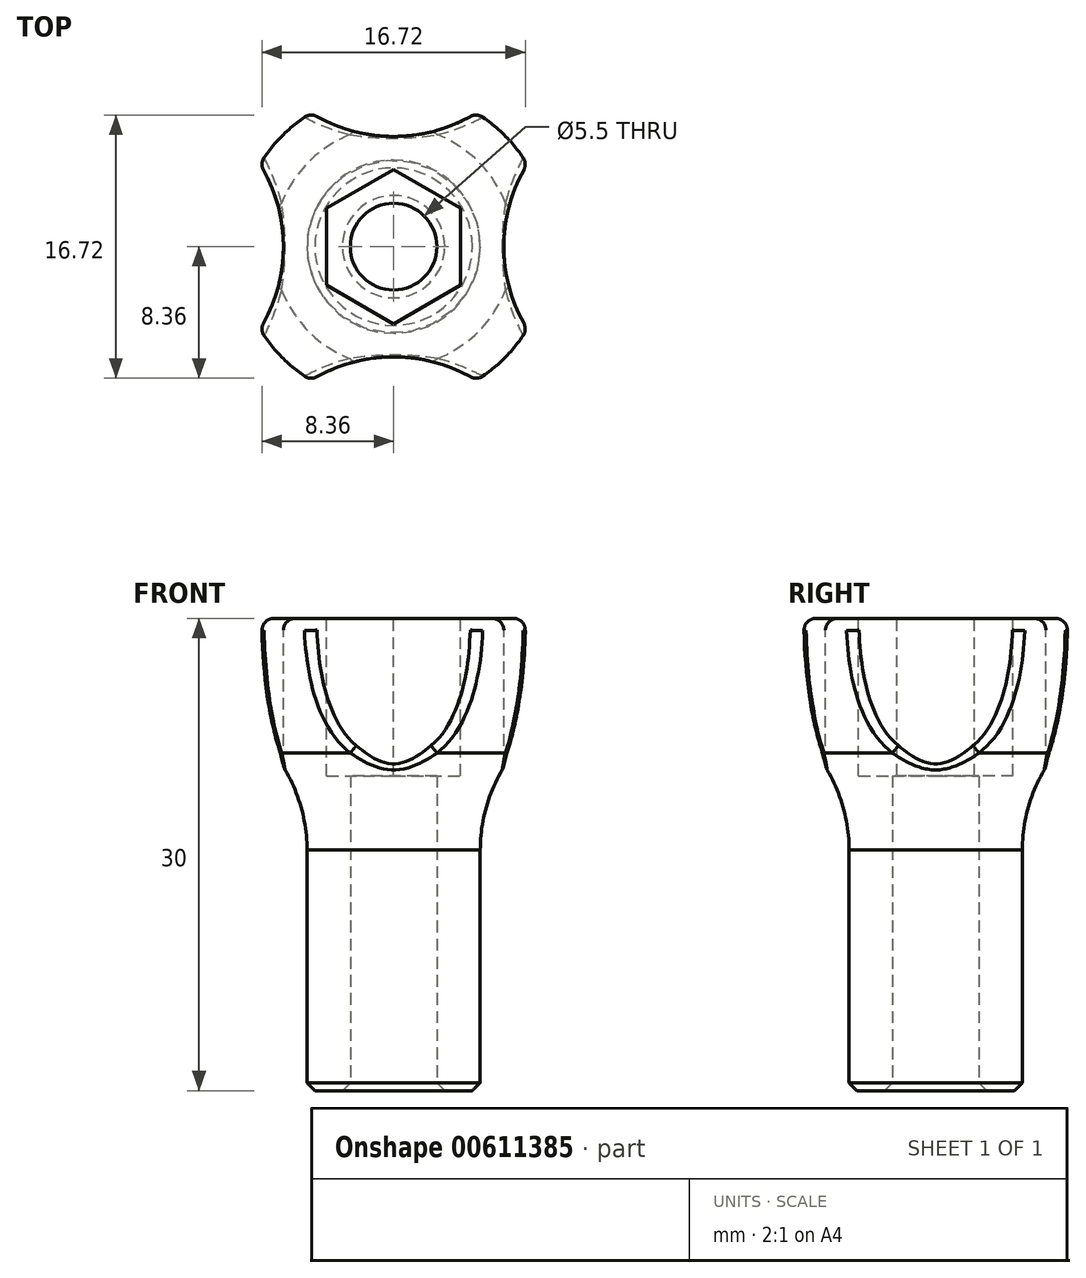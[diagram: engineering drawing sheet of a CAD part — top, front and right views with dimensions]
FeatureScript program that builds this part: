
annotation { "Feature Type Name" : "Feature", "Feature Type Description" : "" }
export const myFeature = defineFeature(function(context is Context, id is Id, definition is map)
    precondition{}
    {
        {
            var Q0;
            Q0=qCreatedBy(makeId("Top.planeOp"),FACE);
            cPlane(context, id + "F0", {"entities" : qUnion([Q0]), "cplaneType" : CPlaneType.OFFSET, "offset" : 30 * mm, "width" : 150 * mm, "height" : 150 * mm});
        }
        {
            var Q0;
            Q0=qCreatedBy(makeId("Top.planeOp"),FACE);
            var sketch = newSketch(context, id + "F1", { "sketchPlane" : qUnion([Q0])});
            skCircle(sketch, "E0", {"center": v(0, 0) * mm, "radius": 2.75 * mm});
            skCircle(sketch, "E1", {"center": v(0, 0) * mm, "radius": 5.5 * mm});
            skSolve(sketch);
        }
        {
            var Q0;
            Q0=makeQuery(id+"F1.imprint","IMPRINT",FACE,{"disambiguationData":[TD([[makeQuery(id+"F1.imprint","IMPRINT",EDGE,{"derivedFrom":sQuery(id+"F1.wireOp",EDGE,"E0")}),-1.0]])]});
            extrude(context, id + "F2", {"entities" : qUnion([Q0]), "depth" : 20 * mm, "offsetDistance" : 25 * mm});
        }
        {
            var Q0;
            Q0=makeQuery(id+"F2.opExtrude","CAP_FACE",FACE,{"disambiguationData":[OSD([sQuery(id+"F1.wireOp",EDGE,"E0"),sQuery(id+"F1.wireOp",EDGE,"E1")])],"isStart":false});
            var sketch = newSketch(context, id + "F3", { "sketchPlane" : qUnion([Q0])});
            skCircle(sketch, "E2", {"center": v(0, 0) * mm, "radius": 5.5 * mm});
            skSolve(sketch);
        }
        {
            var Q0;
            Q0=qCreatedBy(id+"F0.planeOp",FACE);
            var sketch = newSketch(context, id + "F4", { "sketchPlane" : qUnion([Q0])});
            skCircle(sketch, "E3", {"center": v(0, 0) * mm, "radius": 10 * mm});
            skSolve(sketch);
        }
        {
            var Q1;
            Q1 = qSketchRegion(id + "F4", true);
            var Q2;
            Q2 = qSketchRegion(id + "F3", true);
            loft(context, id + "F5", {"operationType" : NewBodyOperationType.ADD, "startCondition" : LoftEndDerivativeType.NORMAL_TO_PROFILE, "startMagnitude" : 2, "endCondition" : LoftEndDerivativeType.TANGENT_TO_PROFILE, "endMagnitude" : 1, "sheetProfilesArray" : [{ "sheetProfileEntities" : qUnion([Q1]) }, { "sheetProfileEntities" : qUnion([Q2]) }]});
        }
        {
            var Q0;
            Q0=makeQuery(id+"F5.boolean.opBoolean","MERGE",EDGE,{"derivedFrom":[makeQuery(id+"F2.opExtrude","CAP_EDGE",EDGE,{"disambiguationData":[OSD([sQuery(id+"F1.wireOp",EDGE,"E1")])],"isStart":false}),makeQuery(id+"F5.opLoft","MID_CAP_EDGE",EDGE,{"disambiguationData":[OSD([sQuery(id+"F3.wireOp",EDGE,"E2")])],"capPos":1.0})]});
            fillet(context, id + "F6", {"entities" : qUnion([Q0]), "radius" : 10 * mm, "tangentPropagation" : true, "allowEdgeOverflow" : false});
        }
        {
            var Q0;
            Q0=qCreatedBy(id+"F0.planeOp",FACE);
            var sketch = newSketch(context, id + "F7", { "sketchPlane" : qUnion([Q0])});
            skCircle(sketch, "E4", {"center": v(0, 17) * mm, "radius": 10 * mm});
            skCircle(sketch, "E5.1.0", {"center": v(-17, 0) * mm, "radius": 10 * mm});
            skCircle(sketch, "E5.2.0", {"center": v(0, -17) * mm, "radius": 10 * mm});
            skCircle(sketch, "E5.3.0", {"center": v(17, 0) * mm, "radius": 10 * mm});
            skPoint(sketch, "E5.center", {"position": v(0, 0) * mm});
            skCircle(sketch, "E6.cCircle", {"center": v(0, 0) * mm, "radius": 4.25 * mm, "construction": true});
            skLineSegment(sketch, "E6.0", {"start": v(4.25, 2.45) * mm, "end": v(4.25, -2.45) * mm});
            skLineSegment(sketch, "E6.1", {"start": v(4.25, -2.45) * mm, "end": v(0, -4.9) * mm});
            skLineSegment(sketch, "E6.2", {"start": v(0, -4.9) * mm, "end": v(-4.25, -2.45) * mm});
            skLineSegment(sketch, "E6.3", {"start": v(-4.25, -2.45) * mm, "end": v(-4.25, 2.45) * mm});
            skLineSegment(sketch, "E6.4", {"start": v(-4.25, 2.45) * mm, "end": v(0, 4.9) * mm});
            skLineSegment(sketch, "E6.5", {"start": v(0, 4.9) * mm, "end": v(4.25, 2.45) * mm});
            skPoint(sketch, "E6.0.midPoint", {"position": v(4.25, 0) * mm});
            skSolve(sketch);
        }
        {
            var Q0;
            Q0=makeQuery(id+"F7.imprint","IMPRINT",FACE,{"disambiguationData":[TD([[makeQuery(id+"F7.imprint","IMPRINT",EDGE,{"derivedFrom":sQuery(id+"F7.wireOp",EDGE,"E5.1.0")}),1.0]])]});
            var Q1;
            Q1=makeQuery(id+"F7.imprint","IMPRINT",FACE,{"disambiguationData":[TD([[makeQuery(id+"F7.imprint","IMPRINT",EDGE,{"derivedFrom":sQuery(id+"F7.wireOp",EDGE,"E4")}),1.0]])]});
            var Q2;
            Q2=makeQuery(id+"F7.imprint","IMPRINT",FACE,{"disambiguationData":[TD([[makeQuery(id+"F7.imprint","IMPRINT",EDGE,{"derivedFrom":sQuery(id+"F7.wireOp",EDGE,"E5.3.0")}),1.0]])]});
            var Q3;
            Q3=makeQuery(id+"F7.imprint","IMPRINT",FACE,{"disambiguationData":[TD([[makeQuery(id+"F7.imprint","IMPRINT",EDGE,{"derivedFrom":sQuery(id+"F7.wireOp",EDGE,"E5.2.0")}),1.0]])]});
            extrude(context, id + "F8", {"entities" : qUnion([Q0, Q1, Q2, Q3]), "operationType" : NewBodyOperationType.REMOVE, "oppositeDirection" : true, "depth" : 25 * mm, "offsetDistance" : 25 * mm});
        }
        {
            var Q0;
            Q0=makeQuery(id+"F7.imprint","IMPRINT",FACE,{"disambiguationData":[TD([[makeQuery(id+"F7.imprint","IMPRINT",EDGE,{"derivedFrom":sQuery(id+"F7.wireOp",EDGE,"E6.0")}),-1.0]])]});
            extrude(context, id + "F9", {"entities" : qUnion([Q0]), "operationType" : NewBodyOperationType.REMOVE, "oppositeDirection" : true, "depth" : 10 * mm, "offsetDistance" : 25 * mm});
        }
        {
            var Q0;
            Q0=makeQuery(id+"F2.opExtrude","CAP_FACE",FACE,{"disambiguationData":[OSD([sQuery(id+"F1.wireOp",EDGE,"E0"),sQuery(id+"F1.wireOp",EDGE,"E1")])],"isStart":true});
            chamfer(context, id + "F10", {"entities" : qUnion([Q0]), "width" : .5 * mm, "tangentPropagation" : true});
        }
        {
            var Q0;
            Q0=makeQuery(id+"F8.boolean.opBoolean","COPY",FACE,{"derivedFrom":makeQuery(id+"F8.opExtrude","SWEPT_FACE",FACE,{"disambiguationData":[OSD([sQuery(id+"F7.wireOp",EDGE,"E5.2.0")])]})});
            var Q1;
            Q1=makeQuery(id+"F8.boolean.opBoolean","COPY",FACE,{"derivedFrom":makeQuery(id+"F8.opExtrude","SWEPT_FACE",FACE,{"disambiguationData":[OSD([sQuery(id+"F7.wireOp",EDGE,"E5.3.0")])]})});
            var Q2;
            Q2=makeQuery(id+"F8.boolean.opBoolean","COPY",FACE,{"derivedFrom":makeQuery(id+"F8.opExtrude","SWEPT_FACE",FACE,{"disambiguationData":[OSD([sQuery(id+"F7.wireOp",EDGE,"E5.1.0")])]})});
            var Q3;
            Q3=makeQuery(id+"F8.boolean.opBoolean","COPY",FACE,{"derivedFrom":makeQuery(id+"F8.opExtrude","SWEPT_FACE",FACE,{"disambiguationData":[OSD([sQuery(id+"F7.wireOp",EDGE,"E4")])]})});
            var Q4;
            {var subQ0=sQuery(id+"F4.wireOp",EDGE,"E3");Q4=makeQuery(id+"F8.boolean.opBoolean","SPLIT",EDGE,{"disambiguationData":[TD([makeQuery(id+"F5.opLoft","SWEPT_FACE",FACE,{"disambiguationData":[OSD([sQuery(id+"F3.wireOp",EDGE,"E2"),subQ0])]}),makeQuery(id+"F5.opLoft","CAP_FACE",FACE,{"disambiguationData":[OSD([makeQuery(id+"F4.imprint","IMPRINT",FACE,{"disambiguationData":[TD([[makeQuery(id+"F4.imprint","IMPRINT",EDGE,{"derivedFrom":subQ0}),1.0]])]})])],"isStart":true}),makeQuery(id+"F8.opExtrude","SWEPT_FACE",FACE,{"disambiguationData":[OSD([sQuery(id+"F7.wireOp",EDGE,"E5.1.0")])]}),makeQuery(id+"F8.opExtrude","SWEPT_FACE",FACE,{"disambiguationData":[OSD([sQuery(id+"F7.wireOp",EDGE,"E5.2.0")])]})])],"derivedFrom":makeQuery(id+"F5.opLoft","MID_CAP_EDGE",EDGE,{"disambiguationData":[OSD([subQ0])],"capPos":0.0})});}
            var Q5;
            {var subQ0=sQuery(id+"F4.wireOp",EDGE,"E3");Q5=makeQuery(id+"F8.boolean.opBoolean","SPLIT",EDGE,{"disambiguationData":[TD([makeQuery(id+"F5.opLoft","SWEPT_FACE",FACE,{"disambiguationData":[OSD([sQuery(id+"F3.wireOp",EDGE,"E2"),subQ0])]}),makeQuery(id+"F5.opLoft","CAP_FACE",FACE,{"disambiguationData":[OSD([makeQuery(id+"F4.imprint","IMPRINT",FACE,{"disambiguationData":[TD([[makeQuery(id+"F4.imprint","IMPRINT",EDGE,{"derivedFrom":subQ0}),1.0]])]})])],"isStart":true}),makeQuery(id+"F8.opExtrude","SWEPT_FACE",FACE,{"disambiguationData":[OSD([sQuery(id+"F7.wireOp",EDGE,"E5.2.0")])]}),makeQuery(id+"F8.opExtrude","SWEPT_FACE",FACE,{"disambiguationData":[OSD([sQuery(id+"F7.wireOp",EDGE,"E5.3.0")])]})])],"derivedFrom":makeQuery(id+"F5.opLoft","MID_CAP_EDGE",EDGE,{"disambiguationData":[OSD([subQ0])],"capPos":0.0})});}
            var Q6;
            {var subQ0=sQuery(id+"F4.wireOp",EDGE,"E3");Q6=makeQuery(id+"F8.boolean.opBoolean","SPLIT",EDGE,{"disambiguationData":[TD([makeQuery(id+"F5.opLoft","SWEPT_FACE",FACE,{"disambiguationData":[OSD([sQuery(id+"F3.wireOp",EDGE,"E2"),subQ0])]}),makeQuery(id+"F5.opLoft","CAP_FACE",FACE,{"disambiguationData":[OSD([makeQuery(id+"F4.imprint","IMPRINT",FACE,{"disambiguationData":[TD([[makeQuery(id+"F4.imprint","IMPRINT",EDGE,{"derivedFrom":subQ0}),1.0]])]})])],"isStart":true}),makeQuery(id+"F8.opExtrude","SWEPT_FACE",FACE,{"disambiguationData":[OSD([sQuery(id+"F7.wireOp",EDGE,"E4")])]}),makeQuery(id+"F8.opExtrude","SWEPT_FACE",FACE,{"disambiguationData":[OSD([sQuery(id+"F7.wireOp",EDGE,"E5.3.0")])]})])],"derivedFrom":makeQuery(id+"F5.opLoft","MID_CAP_EDGE",EDGE,{"disambiguationData":[OSD([subQ0])],"capPos":0.0})});}
            var Q7;
            {var subQ0=sQuery(id+"F4.wireOp",EDGE,"E3");Q7=makeQuery(id+"F8.boolean.opBoolean","SPLIT",EDGE,{"disambiguationData":[TD([makeQuery(id+"F5.opLoft","SWEPT_FACE",FACE,{"disambiguationData":[OSD([sQuery(id+"F3.wireOp",EDGE,"E2"),subQ0])]}),makeQuery(id+"F5.opLoft","CAP_FACE",FACE,{"disambiguationData":[OSD([makeQuery(id+"F4.imprint","IMPRINT",FACE,{"disambiguationData":[TD([[makeQuery(id+"F4.imprint","IMPRINT",EDGE,{"derivedFrom":subQ0}),1.0]])]})])],"isStart":true}),makeQuery(id+"F8.opExtrude","SWEPT_FACE",FACE,{"disambiguationData":[OSD([sQuery(id+"F7.wireOp",EDGE,"E4")])]}),makeQuery(id+"F8.opExtrude","SWEPT_FACE",FACE,{"disambiguationData":[OSD([sQuery(id+"F7.wireOp",EDGE,"E5.1.0")])]})])],"derivedFrom":makeQuery(id+"F5.opLoft","MID_CAP_EDGE",EDGE,{"disambiguationData":[OSD([subQ0])],"capPos":0.0})});}
            var Q8;
            Q8=makeQuery(id+"F9.boolean.opBoolean","COPY",EDGE,{"derivedFrom":makeQuery(id+"F9.opExtrude","CAP_EDGE",EDGE,{"disambiguationData":[OSD([sQuery(id+"F7.wireOp",EDGE,"E6.2")])],"isStart":true})});
            var Q9;
            Q9=makeQuery(id+"F9.boolean.opBoolean","COPY",EDGE,{"derivedFrom":makeQuery(id+"F9.opExtrude","CAP_EDGE",EDGE,{"disambiguationData":[OSD([sQuery(id+"F7.wireOp",EDGE,"E6.3")])],"isStart":true})});
            var Q10;
            Q10=makeQuery(id+"F9.boolean.opBoolean","COPY",EDGE,{"derivedFrom":makeQuery(id+"F9.opExtrude","CAP_EDGE",EDGE,{"disambiguationData":[OSD([sQuery(id+"F7.wireOp",EDGE,"E6.4")])],"isStart":true})});
            var Q11;
            Q11=makeQuery(id+"F9.boolean.opBoolean","COPY",EDGE,{"derivedFrom":makeQuery(id+"F9.opExtrude","CAP_EDGE",EDGE,{"disambiguationData":[OSD([sQuery(id+"F7.wireOp",EDGE,"E6.5")])],"isStart":true})});
            var Q12;
            Q12=makeQuery(id+"F9.boolean.opBoolean","COPY",EDGE,{"derivedFrom":makeQuery(id+"F9.opExtrude","CAP_EDGE",EDGE,{"disambiguationData":[OSD([sQuery(id+"F7.wireOp",EDGE,"E6.0")])],"isStart":true})});
            var Q13;
            Q13=makeQuery(id+"F9.boolean.opBoolean","COPY",EDGE,{"derivedFrom":makeQuery(id+"F9.opExtrude","CAP_EDGE",EDGE,{"disambiguationData":[OSD([sQuery(id+"F7.wireOp",EDGE,"E6.1")])],"isStart":true})});
            var Q14;
            Q14=makeQuery(id+"F2.opExtrude","CAP_EDGE",EDGE,{"disambiguationData":[OSD([sQuery(id+"F1.wireOp",EDGE,"E0")])],"isStart":false});
            fillet(context, id + "F11", {"entities" : qUnion([Q0, Q1, Q2, Q3, Q4, Q5, Q6, Q7, Q8, Q9, Q10, Q11, Q12, Q13, Q14]), "radius" : 0.75 * mm, "tangentPropagation" : true, "allowEdgeOverflow" : false});
        }
    });
